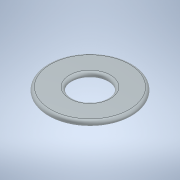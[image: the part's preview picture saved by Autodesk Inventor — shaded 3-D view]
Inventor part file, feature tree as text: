
AUTODESK INVENTOR PART (.ipt)
format: ipt  version: 2021 (Build 250183000, 183)  size: 129,536 bytes
history: native  units: mm
features: extrude x1, fillet x1, sketch x1
ambient origin geometry x8: Origin, YZ Plane, XZ Plane, XY Plane, X Axis, Y Axis, Z Axis, Center Point
bodies: Solid1 (feature_tree)
feature tree (3):
  extrude  "Extrusion1"  Depth=0.625mm
  fillet  "Fillet1"  Radius=1.25mm
  sketch  "Sketch1"  dims[d0=8.0mm d1=19.0mm d2=1.25mm d3=0.0mm d4=0.625mm]
